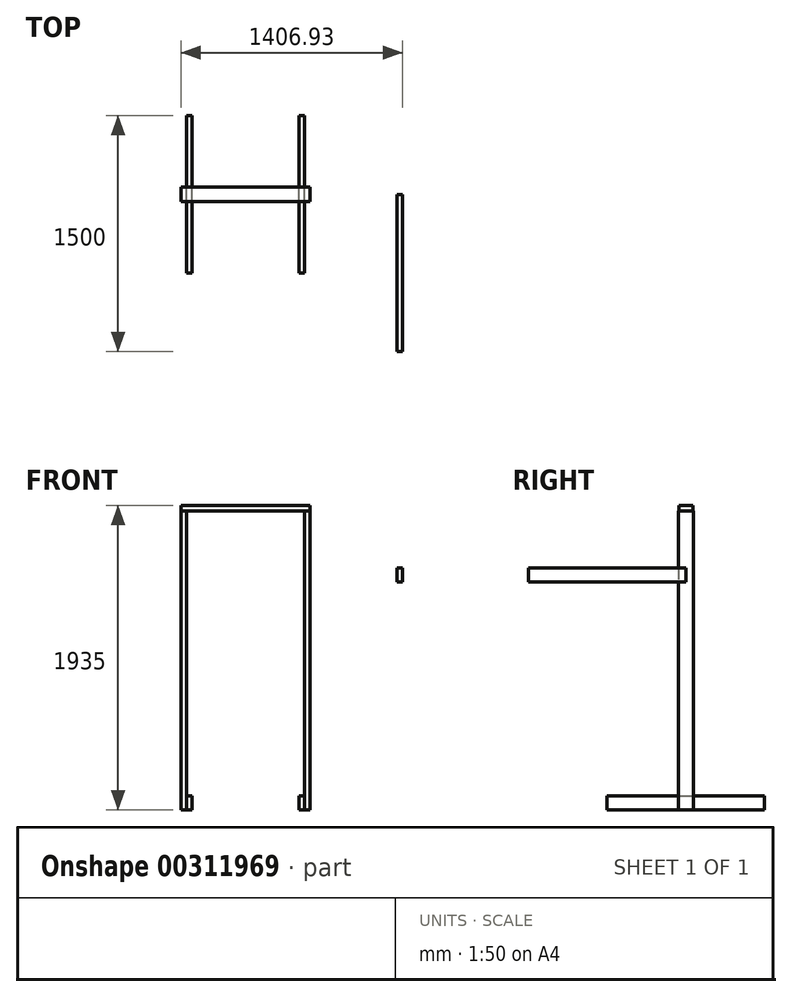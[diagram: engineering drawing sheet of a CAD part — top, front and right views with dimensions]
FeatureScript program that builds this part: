
annotation { "Feature Type Name" : "Feature", "Feature Type Description" : "" }
export const myFeature = defineFeature(function(context is Context, id is Id, definition is map)
    precondition{}
    {
        {
            var Q0;
            Q0=qCreatedBy(makeId("Front.planeOp"),FACE);
            var sketch = newSketch(context, id + "F0", { "sketchPlane" : qUnion([Q0])});
            skLineSegment(sketch, "E0.bottom", {"start": v(961.93, 587.65) * mm, "end": v(996.93, 587.65) * mm});
            skLineSegment(sketch, "E0.top", {"start": v(961.93, 497.65) * mm, "end": v(996.93, 497.65) * mm});
            skLineSegment(sketch, "E0.left", {"start": v(961.93, 587.65) * mm, "end": v(961.93, 497.65) * mm});
            skLineSegment(sketch, "E0.right", {"start": v(996.93, 587.65) * mm, "end": v(996.93, 497.65) * mm});
            skLineSegment(sketch, "E1.bottom", {"start": v(-375, 950) * mm, "end": v(375, 950) * mm});
            skLineSegment(sketch, "E1.top", {"start": v(-375, -950) * mm, "end": v(-340, -950) * mm, "construction": true});
            skLineSegment(sketch, "E1.left", {"start": v(-375, 950) * mm, "end": v(-375, -950) * mm});
            skLineSegment(sketch, "E1.right", {"start": v(375, 950) * mm, "end": v(375, -950) * mm});
            skPoint(sketch, "E1.middle", {"position": v(0, 0) * mm});
            skLineSegment(sketch, "E2.bottom", {"start": v(-375, -950) * mm, "end": v(-340, -950) * mm});
            skLineSegment(sketch, "E2.top", {"start": v(-375, -860) * mm, "end": v(-340, -860) * mm});
            skLineSegment(sketch, "E2.left", {"start": v(-375, -950) * mm, "end": v(-375, -860) * mm});
            skLineSegment(sketch, "E2.right", {"start": v(-340, -950) * mm, "end": v(-340, -860) * mm});
            skLineSegment(sketch, "E3.MirrorCS", {"start": v(340, -950) * mm, "end": v(340, -860) * mm});
            skLineSegment(sketch, "E4.MirrorCS", {"start": v(375, -860) * mm, "end": v(340, -860) * mm});
            skLineSegment(sketch, "E5.MirrorCS", {"start": v(375, -950) * mm, "end": v(375, -860) * mm});
            skLineSegment(sketch, "E6.trimOffspring", {"start": v(340, -950) * mm, "end": v(375, -950) * mm, "construction": true});
            skLineSegment(sketch, "E7", {"start": v(340, -950) * mm, "end": v(375, -950) * mm});
            skSolve(sketch);
        }
        {
            var Q0;
            Q0=makeQuery(id+"F0.imprint","IMPRINT",FACE,{"disambiguationData":[TD([[makeQuery(id+"F0.imprint","IMPRINT",EDGE,{"derivedFrom":sQuery(id+"F0.wireOp",EDGE,"E0.bottom")}),-1.0]])]});
            extrude(context, id + "F1", {"entities" : qUnion([Q0]), "depth" : 1000 * mm, "offsetDistance" : 25 * mm});
        }
        {
            var Q0;
            Q0=makeQuery(id+"F0.imprint","IMPRINT",FACE,{"disambiguationData":[TD([[makeQuery(id+"F0.imprint","IMPRINT",EDGE,{"derivedFrom":sQuery(id+"F0.wireOp",EDGE,"E2.bottom")}),1.0]])]});
            var Q1;
            Q1=makeQuery(id+"F0.imprint","IMPRINT",FACE,{"disambiguationData":[TD([[makeQuery(id+"F0.imprint","IMPRINT",EDGE,{"derivedFrom":sQuery(id+"F0.wireOp",EDGE,"E3.MirrorCS")}),-1.0]])]});
            extrude(context, id + "F2", {"entities" : qUnion([Q0, Q1]), "endBound" : BoundingType.SYMMETRIC, "depth" : 1000 * mm, "offsetDistance" : 25 * mm});
        }
        {
            var Q0;
            Q0=sQuery(id+"F0.wireOp",EDGE,"E1.right");
            var Q1;
            Q1=sQuery(id+"F0.wireOp",VERTEX,"E6.trimOffspring.end");
            cPlane(context, id + "F3", {"entities" : qUnion([Q0, Q1]), "cplaneType" : CPlaneType.LINE_POINT, "offset" : 25 * mm, "width" : 150 * mm, "height" : 150 * mm});
        }
        {
            var Q0;
            Q0=qCreatedBy(id+"F3.planeOp",FACE);
            var sketch = newSketch(context, id + "F4", { "sketchPlane" : qUnion([Q0])});
            skLineSegment(sketch, "E8.bottom", {"start": v(375, 47.5) * mm, "end": v(410, 47.5) * mm});
            skLineSegment(sketch, "E8.top", {"start": v(375, -47.5) * mm, "end": v(410, -47.5) * mm});
            skLineSegment(sketch, "E8.left", {"start": v(375, 47.5) * mm, "end": v(375, -47.5) * mm});
            skLineSegment(sketch, "E8.right", {"start": v(410, 47.5) * mm, "end": v(410, -47.5) * mm});
            skPoint(sketch, "E8.middle", {"position": v(392.5, 0) * mm});
            skLineSegment(sketch, "E9.MirrorCS", {"start": v(-375, 47.5) * mm, "end": v(-375, -47.5) * mm});
            skLineSegment(sketch, "E10.MirrorCS", {"start": v(-375, 47.5) * mm, "end": v(-410, 47.5) * mm});
            skLineSegment(sketch, "E11.MirrorCS", {"start": v(-410, 47.5) * mm, "end": v(-410, -47.5) * mm});
            skLineSegment(sketch, "E12.MirrorCS", {"start": v(-375, -47.5) * mm, "end": v(-410, -47.5) * mm});
            skSolve(sketch);
        }
        {
            var Q0;
            Q0=makeQuery(id+"F4.imprint","IMPRINT",FACE,{"disambiguationData":[TD([[makeQuery(id+"F4.imprint","IMPRINT",EDGE,{"derivedFrom":sQuery(id+"F4.wireOp",EDGE,"E8.bottom")}),-1.0]])]});
            var Q1;
            Q1=makeQuery(id+"F4.imprint","IMPRINT",FACE,{"disambiguationData":[TD([[makeQuery(id+"F4.imprint","IMPRINT",EDGE,{"derivedFrom":sQuery(id+"F4.wireOp",EDGE,"E9.MirrorCS")}),-1.0]])]});
            var Q2;
            Q2=sQuery(id+"F0.wireOp",VERTEX,"E1.bottom.end");
            extrude(context, id + "F5", {"entities" : qUnion([Q0, Q1]), "endBound" : BoundingType.UP_TO_VERTEX, "oppositeDirection" : true, "depth" : 1500 * mm, "endBoundEntityVertex" : qUnion([Q2]), "offsetDistance" : 25 * mm});
        }
        {
            var Q0;
            Q0=qCreatedBy(makeId("Right.planeOp"),FACE);
            var sketch = newSketch(context, id + "F6", { "sketchPlane" : qUnion([Q0])});
            skPoint(sketch, "E13.0", {"position": v(0, 950) * mm});
            skLineSegment(sketch, "E14.bottom", {"start": v(45, 915) * mm, "end": v(-45, 915) * mm, "construction": true});
            skLineSegment(sketch, "E14.top", {"start": v(45, 950) * mm, "end": v(-45, 950) * mm});
            skLineSegment(sketch, "E14.left", {"start": v(45, 915) * mm, "end": v(45, 950) * mm, "construction": true});
            skLineSegment(sketch, "E14.right", {"start": v(-45, 915) * mm, "end": v(-45, 950) * mm, "construction": true});
            skPoint(sketch, "E14.middle", {"position": v(0, 932.5) * mm});
            skLineSegment(sketch, "E15.MirrorCS", {"start": v(-45, 985) * mm, "end": v(-45, 950) * mm});
            skLineSegment(sketch, "E16.MirrorCS", {"start": v(45, 985) * mm, "end": v(-45, 985) * mm});
            skLineSegment(sketch, "E17.MirrorCS", {"start": v(45, 985) * mm, "end": v(45, 950) * mm});
            skSolve(sketch);
        }
        {
            var Q0;
            Q0=makeQuery(id+"F6.imprint","IMPRINT",FACE,{"disambiguationData":[TD([[makeQuery(id+"F6.imprint","IMPRINT",EDGE,{"derivedFrom":sQuery(id+"F6.wireOp",EDGE,"E14.top")}),-1.0]])]});
            var Q1;
            Q1=makeQuery(id+"F5.opExtrude","SWEPT_FACE",FACE,{"disambiguationData":[OSD([sQuery(id+"F4.wireOp",EDGE,"E8.right")])]});
            var Q2;
            Q2=makeQuery(id+"F5.opExtrude","SWEPT_BODY",BODY,{"disambiguationData":[OSD([sQuery(id+"F4.wireOp",EDGE,"E8.bottom"),sQuery(id+"F4.wireOp",EDGE,"E8.top"),sQuery(id+"F4.wireOp",EDGE,"E8.left"),sQuery(id+"F4.wireOp",EDGE,"E8.right")])]});
            var Q3;
            Q3=makeQuery(id+"F5.opExtrude","SWEPT_FACE",FACE,{"disambiguationData":[OSD([sQuery(id+"F4.wireOp",EDGE,"E11.MirrorCS")])]});
            extrude(context, id + "F7", {"entities" : qUnion([Q0]), "endBound" : BoundingType.UP_TO_SURFACE, "depth" : 25 * mm, "endBoundEntityFace" : qUnion([Q1]), "endBoundEntityBody" : qUnion([Q2]), "offsetDistance" : 25 * mm, "hasSecondDirection" : true, "secondDirectionBound" : SecondDirectionBoundingType.UP_TO_SURFACE, "secondDirectionOppositeDirection" : true, "secondDirectionDepth" : 25 * mm, "secondDirectionBoundEntityFace" : qUnion([Q3])});
        }
    });
